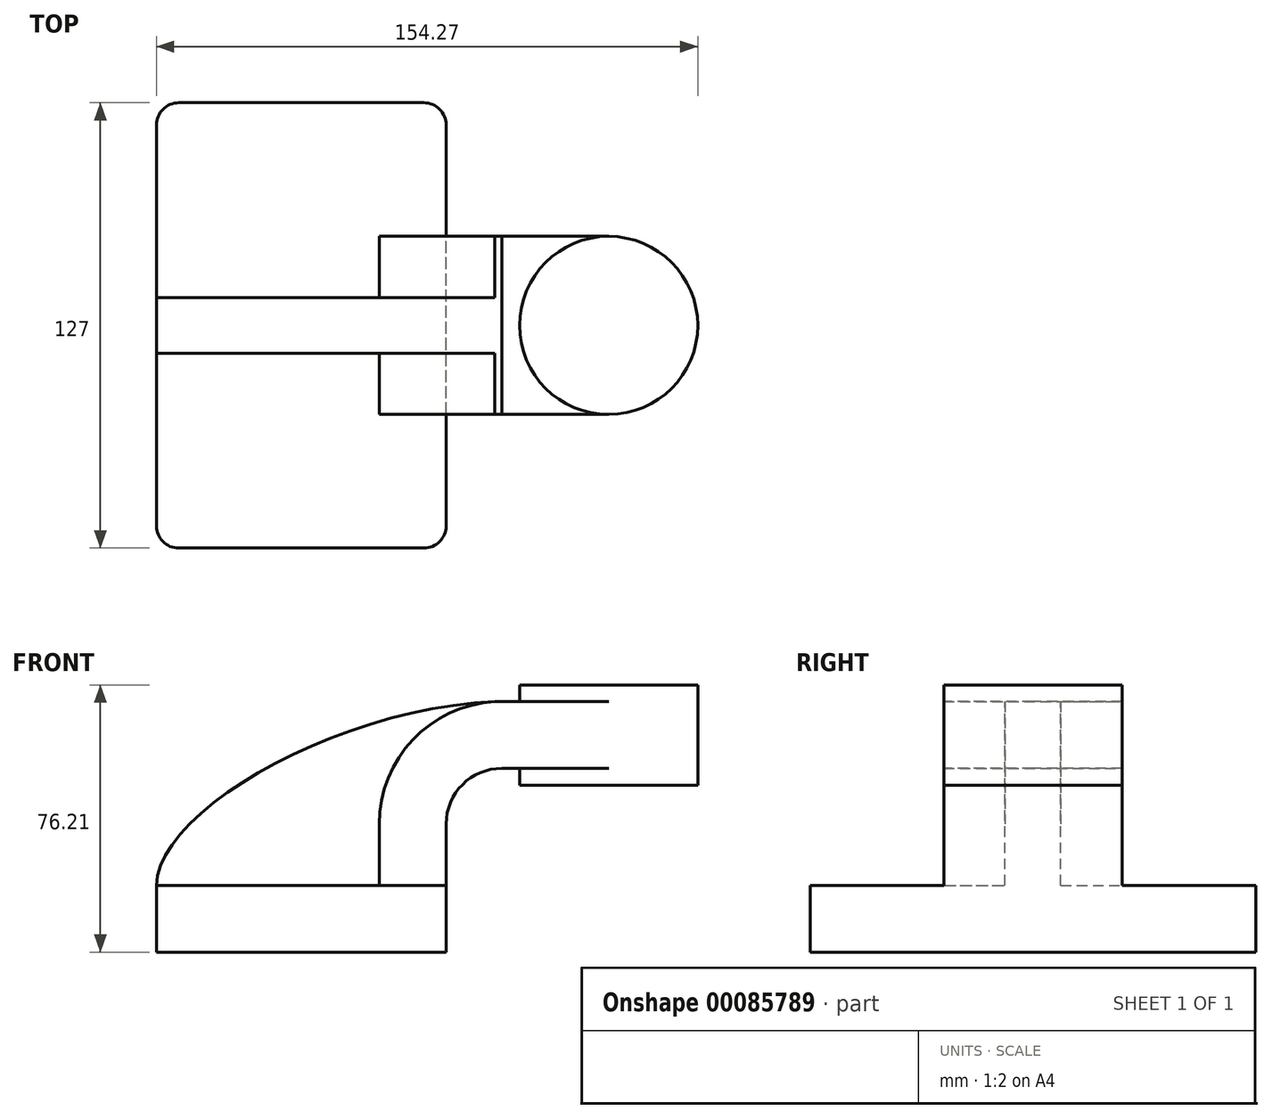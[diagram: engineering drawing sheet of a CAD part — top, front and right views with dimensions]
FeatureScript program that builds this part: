
annotation { "Feature Type Name" : "Feature", "Feature Type Description" : "" }
export const myFeature = defineFeature(function(context is Context, id is Id, definition is map)
    precondition{}
    {
        {
            var Q0;
            Q0=qCreatedBy(makeId("Front.planeOp"),FACE);
            var sketch = newSketch(context, id + "F0", { "sketchPlane" : qUnion([Q0])});
            skLineSegment(sketch, "E0.bottom", {"start": v(-41.28, -9.53) * mm, "end": v(41.28, -9.53) * mm});
            skLineSegment(sketch, "E0.top", {"start": v(-41.28, 9.53) * mm, "end": v(41.28, 9.53) * mm});
            skLineSegment(sketch, "E0.left", {"start": v(-41.28, -9.53) * mm, "end": v(-41.28, 9.53) * mm});
            skLineSegment(sketch, "E0.right", {"start": v(41.28, -9.53) * mm, "end": v(41.28, 9.53) * mm});
            skPoint(sketch, "E0.middle", {"position": v(0, 0) * mm});
            skLineSegment(sketch, "E1.bottom", {"start": v(112.99, 38.1) * mm, "end": v(62.19, 38.1) * mm});
            skLineSegment(sketch, "E1.top", {"start": v(112.99, 66.67) * mm, "end": v(62.19, 66.67) * mm});
            skLineSegment(sketch, "E1.left", {"start": v(112.99, 38.1) * mm, "end": v(112.99, 66.67) * mm});
            skLineSegment(sketch, "E1.right", {"start": v(62.19, 38.1) * mm, "end": v(62.19, 66.67) * mm});
            skPoint(sketch, "E1.middle", {"position": v(87.59, 52.39) * mm});
            skLineSegment(sketch, "E2", {"start": v(41.28, 9.53) * mm, "end": v(41.28, 27) * mm});
            skArc(sketch, "E3", {"start": v(41.27, 27) * mm, "mid": v(45.92, 38.23) * mm, "end": v(57.15, 42.88) * mm});
            skLineSegment(sketch, "E4", {"start": v(57.15, 42.88) * mm, "end": v(87.59, 42.88) * mm});
            skLineSegment(sketch, "E5.0", {"start": v(57.15, 61.93) * mm, "end": v(87.59, 61.93) * mm});
            skArc(sketch, "E5.1", {"start": v(22.22, 27) * mm, "mid": v(32.45, 51.7) * mm, "end": v(57.15, 61.93) * mm});
            skLineSegment(sketch, "E5.2", {"start": v(22.22, 9.53) * mm, "end": v(22.22, 27) * mm});
            skLineSegment(sketch, "E6", {"start": v(87.59, 38.1) * mm, "end": v(87.59, 66.67) * mm});
            skFitSpline(sketch, "E7", {"points": [v(-41.28, 9.52) * mm, v(57.15, 61.93) * mm], "startDerivative": vector(0.25, 64.08) * mm, "endDerivative": vector(136.27, 2.64) * mm});
            skSolve(sketch);
        }
        {
            var Q0;
            Q0=makeQuery(id+"F0.imprint","IMPRINT",FACE,{"disambiguationData":[TD([[makeQuery(id+"F0.imprint","IMPRINT",EDGE,{"derivedFrom":sQuery(id+"F0.wireOp",EDGE,"E0.bottom")}),1.0]])]});
            extrude(context, id + "F1", {"entities" : qUnion([Q0]), "endBound" : BoundingType.SYMMETRIC, "depth" : 127 * mm});
        }
        {
            var Q0;
            {var subQ1=sQuery(id+"F0.wireOp",EDGE,"E2");Q0=makeQuery(id+"F0.imprint","IMPRINT",FACE,{"disambiguationData":[TD([[makeQuery(id+"F0.imprint","IMPRINT",EDGE,{"derivedFrom":subQ1}),1.0]])]});}
            var Q1;
            {var subQ0=sQuery(id+"F0.wireOp",EDGE,"E4");var subQ1=sQuery(id+"F0.wireOp",EDGE,"E1.right");var subQ2=makeQuery(id+"F0.imprint","INTERSECT",VERTEX,{"derivedFrom":[subQ1,subQ0]});Q1=makeQuery(id+"F0.imprint","IMPRINT",FACE,{"disambiguationData":[TD([[makeQuery(id+"F0.imprint","IMPRINT",EDGE,{"disambiguationData":[TD([[subQ2,-1.0]])],"derivedFrom":subQ1}),-1.0]])]});}
            extrude(context, id + "F2", {"entities" : qUnion([Q0, Q1]), "operationType" : NewBodyOperationType.ADD, "endBound" : BoundingType.SYMMETRIC, "depth" : 50.8 * mm});
        }
        {
            var Q0;
            {var subQ3=sQuery(id+"F0.wireOp",EDGE,"E5.2");Q0=makeQuery(id+"F0.imprint","IMPRINT",FACE,{"disambiguationData":[TD([[makeQuery(id+"F0.imprint","IMPRINT",EDGE,{"derivedFrom":subQ3}),1.0]])]});}
            extrude(context, id + "F3", {"entities" : qUnion([Q0]), "operationType" : NewBodyOperationType.ADD, "endBound" : BoundingType.SYMMETRIC, "depth" : 15.88 * mm});
        }
        {
            var Q0;
            {var subQ0=sQuery(id+"F0.wireOp",EDGE,"E1.left");Q0=makeQuery(id+"F0.imprint","IMPRINT",FACE,{"disambiguationData":[TD([[makeQuery(id+"F0.imprint","IMPRINT",EDGE,{"derivedFrom":subQ0}),1.0]])]});}
            var Q1;
            Q1=sQuery(id+"F0.wireOp",EDGE,"E6");
            revolve(context, id + "F4", {"operationType" : NewBodyOperationType.ADD, "entities" : qUnion([Q0]), "axis" : qUnion([Q1]), "revolveType" : RevolveType.FULL});
        }
        {
            var Q0;
            Q0=makeQuery(id+"F1.opExtrude","CAP_EDGE",EDGE,{"disambiguationData":[OSD([sQuery(id+"F0.wireOp",EDGE,"E0.left")])],"isStart":false});
            var Q1;
            Q1=makeQuery(id+"F1.opExtrude","CAP_EDGE",EDGE,{"disambiguationData":[OSD([sQuery(id+"F0.wireOp",EDGE,"E0.right")])],"isStart":false});
            var Q2;
            Q2=makeQuery(id+"F1.opExtrude","CAP_EDGE",EDGE,{"disambiguationData":[OSD([sQuery(id+"F0.wireOp",EDGE,"E0.right")])],"isStart":true});
            var Q3;
            Q3=makeQuery(id+"F1.opExtrude","CAP_EDGE",EDGE,{"disambiguationData":[OSD([sQuery(id+"F0.wireOp",EDGE,"E0.left")])],"isStart":true});
            fillet(context, id + "F5", {"entities" : qUnion([Q0, Q1, Q2, Q3]), "radius" : 6.35 * mm, "tangentPropagation" : true, "allowEdgeOverflow" : false});
        }
    });
